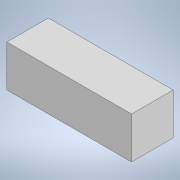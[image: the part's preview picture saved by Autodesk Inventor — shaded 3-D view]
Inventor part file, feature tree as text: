
AUTODESK INVENTOR PART (.ipt)
format: ipt  version: 2022 (Build 260153000, 153)  size: 91,136 bytes
history: native  units: in
note: dims shown in document units (in); Inventor stores cm internally (conversion verified against a paired STEP export)
features: extrude x1, sketch x1
ambient origin geometry x8: Origin, YZ Plane, XZ Plane, XY Plane, X Axis, Y Axis, Z Axis, Center Point
bodies: Body1 (feature_tree)
feature tree (2):
  extrude  "Extrusion2"  Depth=0.3in
  sketch  "Sketch1"  dims[d6=0.05in d7=0.05in d8=0.05in d9=0.05in d10=0.3in d11=0.0in d12=0.5in d13=0.0344in d14=0.5in d15=0.0344in]
